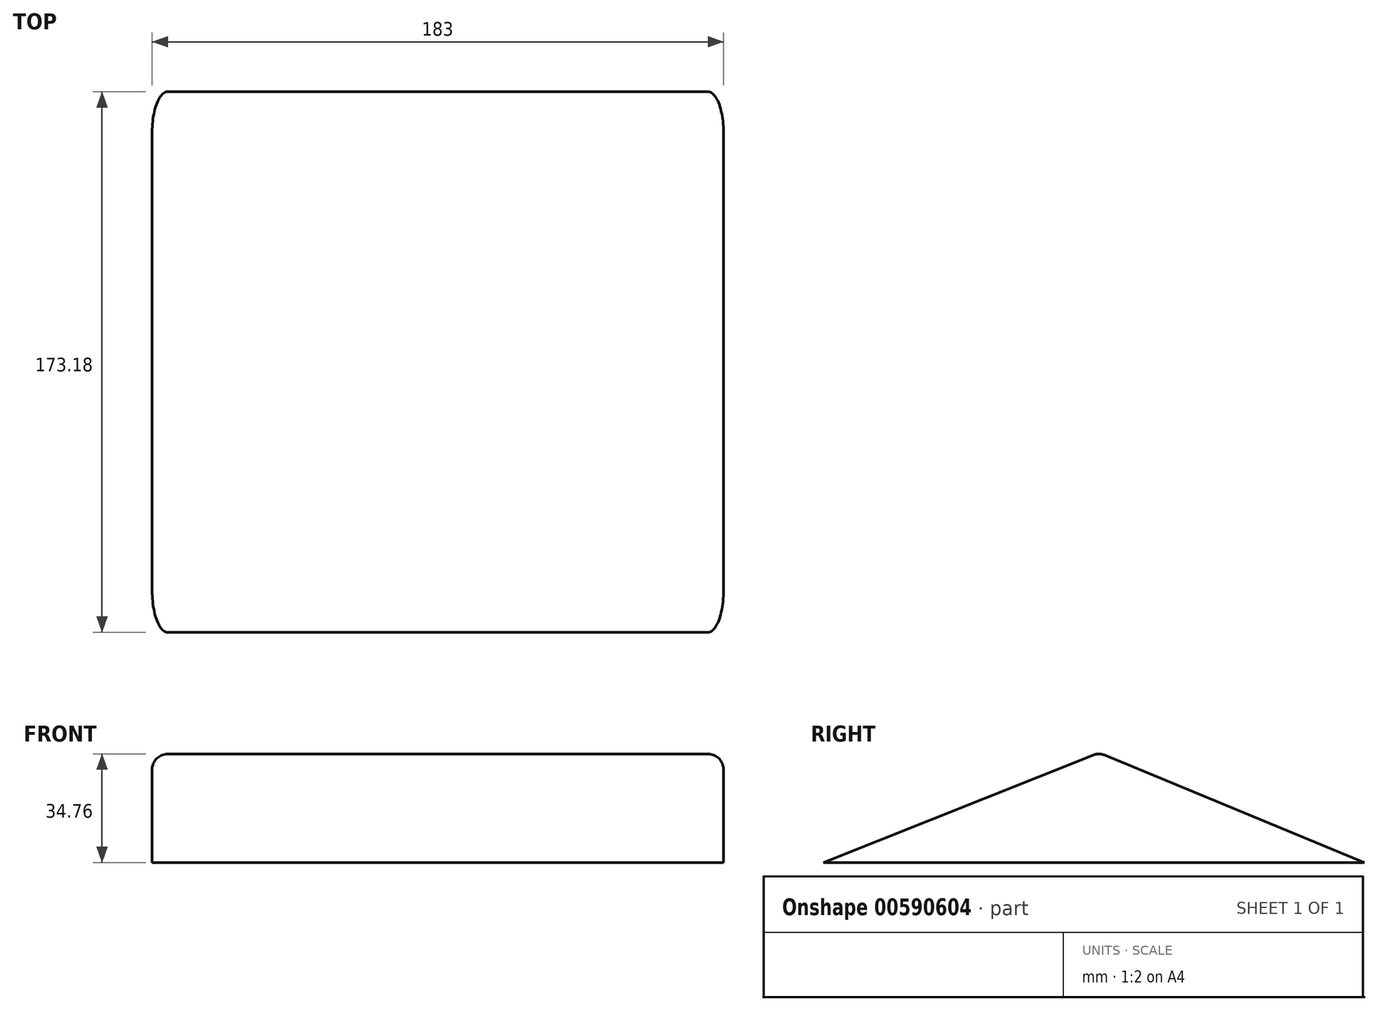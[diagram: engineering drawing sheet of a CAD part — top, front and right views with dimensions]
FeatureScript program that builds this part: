
annotation { "Feature Type Name" : "Feature", "Feature Type Description" : "" }
export const myFeature = defineFeature(function(context is Context, id is Id, definition is map)
    precondition{}
    {
        {
            var Q0;
            Q0=qCreatedBy(makeId("Top.planeOp"),FACE);
            var sketch = newSketch(context, id + "F0", { "sketchPlane" : qUnion([Q0])});
            skLineSegment(sketch, "E0.bottom", {"start": v(60, 85) * mm, "end": v(-60, 85) * mm});
            skLineSegment(sketch, "E0.top", {"start": v(60, -85) * mm, "end": v(-60, -85) * mm});
            skLineSegment(sketch, "E0.left", {"start": v(60, 85) * mm, "end": v(60, -85) * mm});
            skLineSegment(sketch, "E0.right", {"start": v(-60, 85) * mm, "end": v(-60, -85) * mm});
            skPoint(sketch, "E0.middle", {"position": v(0, 0) * mm});
            skSolve(sketch);
        }
        {
            var Q0;
            Q0=qCreatedBy(makeId("Right.planeOp"),FACE);
            cPlane(context, id + "F1", {"entities" : qUnion([Q0]), "cplaneType" : CPlaneType.OFFSET, "offset" : 0.6 * mm, "oppositeDirection" : true, "width" : 150 * mm, "height" : 150 * mm});
        }
        {
            var Q0;
            Q0=qCreatedBy(id+"F1.planeOp",FACE);
            var sketch = newSketch(context, id + "F2", { "sketchPlane" : qUnion([Q0])});
            skLineSegment(sketch, "E1", {"start": v(84.95, 0) * mm, "end": v(0, 35.15) * mm});
            skLineSegment(sketch, "E2", {"start": v(-88.23, 0) * mm, "end": v(0, 35.15) * mm});
            skLineSegment(sketch, "E3", {"start": v(-88.23, 0) * mm, "end": v(87.15, 0) * mm});
            skSolve(sketch);
        }
        {
            var Q0;
            {var subQ0=sQuery(id+"F2.wireOp",EDGE,"E1");Q0=makeQuery(id+"F2.imprint","IMPRINT",FACE,{"disambiguationData":[TD([[makeQuery(id+"F2.imprint","IMPRINT",EDGE,{"derivedFrom":subQ0}),1.0]])]});}
            extrude(context, id + "F3", {"entities" : qUnion([Q0]), "oppositeDirection" : true, "depth" : 183 * mm, "offsetDistance" : 25 * mm});
        }
        {
            var Q0;
            Q0=makeQuery(id+"F3.opExtrude","CAP_EDGE",EDGE,{"disambiguationData":[OSD([sQuery(id+"F2.wireOp",EDGE,"E2")])],"isStart":true});
            var Q1;
            Q1=makeQuery(id+"F3.opExtrude","CAP_EDGE",EDGE,{"disambiguationData":[OSD([sQuery(id+"F2.wireOp",EDGE,"E2")])],"isStart":false});
            var Q2;
            Q2=makeQuery(id+"F3.opExtrude","CAP_EDGE",EDGE,{"disambiguationData":[OSD([sQuery(id+"F2.wireOp",EDGE,"E1")])],"isStart":true});
            var Q3;
            Q3=makeQuery(id+"F3.opExtrude","SWEPT_EDGE",EDGE,{"disambiguationData":[OSD([sQuery(id+"F2.wireOp",EDGE,"E1"),sQuery(id+"F2.wireOp",EDGE,"E2")])]});
            var Q4;
            Q4=makeQuery(id+"F3.opExtrude","CAP_EDGE",EDGE,{"disambiguationData":[OSD([sQuery(id+"F2.wireOp",EDGE,"E1")])],"isStart":false});
            fillet(context, id + "F4", {"entities" : qUnion([Q0, Q1, Q2, Q3, Q4]), "radius" : 5 * mm, "tangentPropagation" : true, "allowEdgeOverflow" : false});
        }
    });
